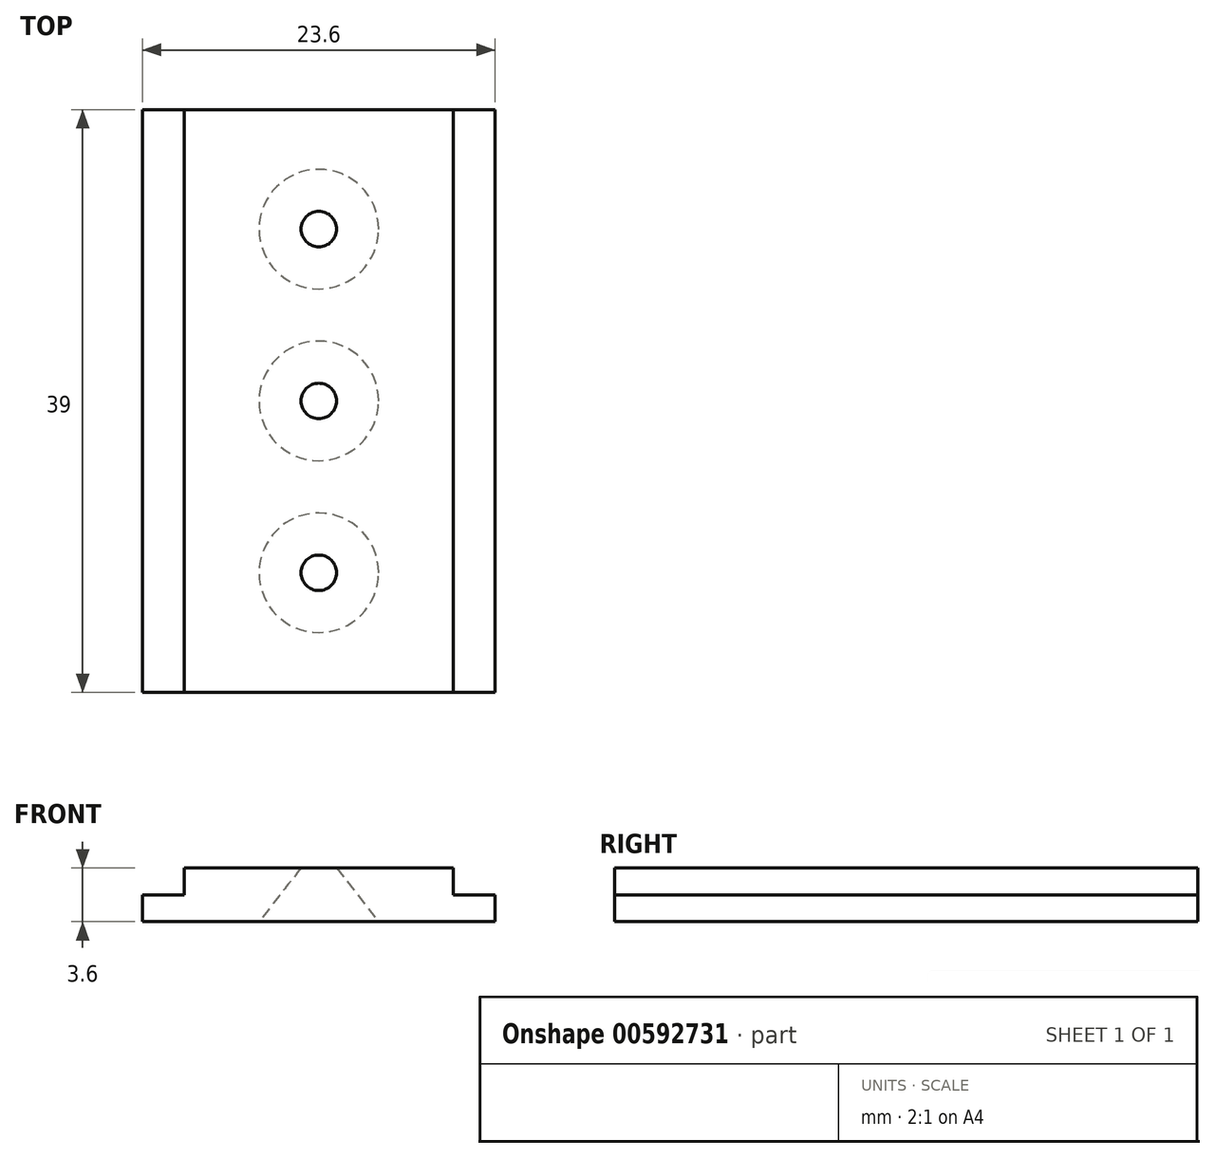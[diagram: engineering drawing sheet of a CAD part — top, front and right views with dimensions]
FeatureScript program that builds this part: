
annotation { "Feature Type Name" : "Feature", "Feature Type Description" : "" }
export const myFeature = defineFeature(function(context is Context, id is Id, definition is map)
    precondition{}
    {
        {
            var Q0;
            Q0=qCreatedBy(makeId("Front.planeOp"),FACE);
            var sketch = newSketch(context, id + "F0", { "sketchPlane" : qUnion([Q0])});
            skLineSegment(sketch, "E0.bottom", {"start": v(-10.4, 1.8) * mm, "end": v(7.6, 1.8) * mm});
            skPoint(sketch, "E0.middle", {"position": v(0, 0) * mm});
            skLineSegment(sketch, "E1", {"start": v(7.6, 1.8) * mm, "end": v(7.6, 0) * mm});
            skLineSegment(sketch, "E2", {"start": v(7.6, 0) * mm, "end": v(10.4, 0) * mm});
            skLineSegment(sketch, "E3", {"start": v(-10.4, 1.8) * mm, "end": v(-10.4, 0) * mm});
            skLineSegment(sketch, "E4", {"start": v(-10.4, 0) * mm, "end": v(-13.2, 0) * mm});
            skLineSegment(sketch, "E5", {"start": v(-13.2, 0) * mm, "end": v(-13.2, -1.8) * mm});
            skLineSegment(sketch, "E6", {"start": v(10.4, 0) * mm, "end": v(10.4, -1.8) * mm});
            skLineSegment(sketch, "E7", {"start": v(10.4, -1.8) * mm, "end": v(-13.2, -1.8) * mm});
            skSolve(sketch);
        }
        {
            var Q0;
            Q0 = qSketchRegion(id + "F0", true);
            extrude(context, id + "F1", {"entities" : qUnion([Q0]), "oppositeDirection" : true, "depth" : 39 * mm, "offsetDistance" : 25 * mm});
        }
        {
            var Q0;
            Q0=makeQuery(id+"F1.opExtrude","SWEPT_FACE",FACE,{"disambiguationData":[OSD([sQuery(id+"F0.wireOp",EDGE,"E7")])]});
            var sketch = newSketch(context, id + "F2", { "sketchPlane" : qUnion([Q0])});
            skCircle(sketch, "E8", {"center": v(-1.4, -31) * mm, "radius": 4 * mm});
            skCircle(sketch, "E9", {"center": v(-1.4, -19.5) * mm, "radius": 4 * mm});
            skCircle(sketch, "E10", {"center": v(-1.4, -8) * mm, "radius": 4 * mm});
            skLineSegment(sketch, "E11", {"start": v(-1.4, 0) * mm, "end": v(-1.4, -39) * mm, "construction": true});
            skSolve(sketch);
        }
        {
            var Q0;
            Q0 = qSketchRegion(id + "F2", true);
            var Q1;
            Q1=makeQuery(id+"F1.opExtrude","SWEPT_FACE",FACE,{"disambiguationData":[OSD([sQuery(id+"F0.wireOp",EDGE,"E0.bottom")])]});
            extrude(context, id + "F3", {"entities" : qUnion([Q0]), "operationType" : NewBodyOperationType.REMOVE, "endBound" : BoundingType.UP_TO_SURFACE, "oppositeDirection" : true, "depth" : 5 * mm, "endBoundEntityFace" : qUnion([Q1]), "hasOffset" : true, "offsetDistance" : 0 * mm, "offsetOppositeDirection" : true, "hasDraft" : true, "draftAngle" : 38 * degree, "draftPullDirection" : true});
        }
    });
